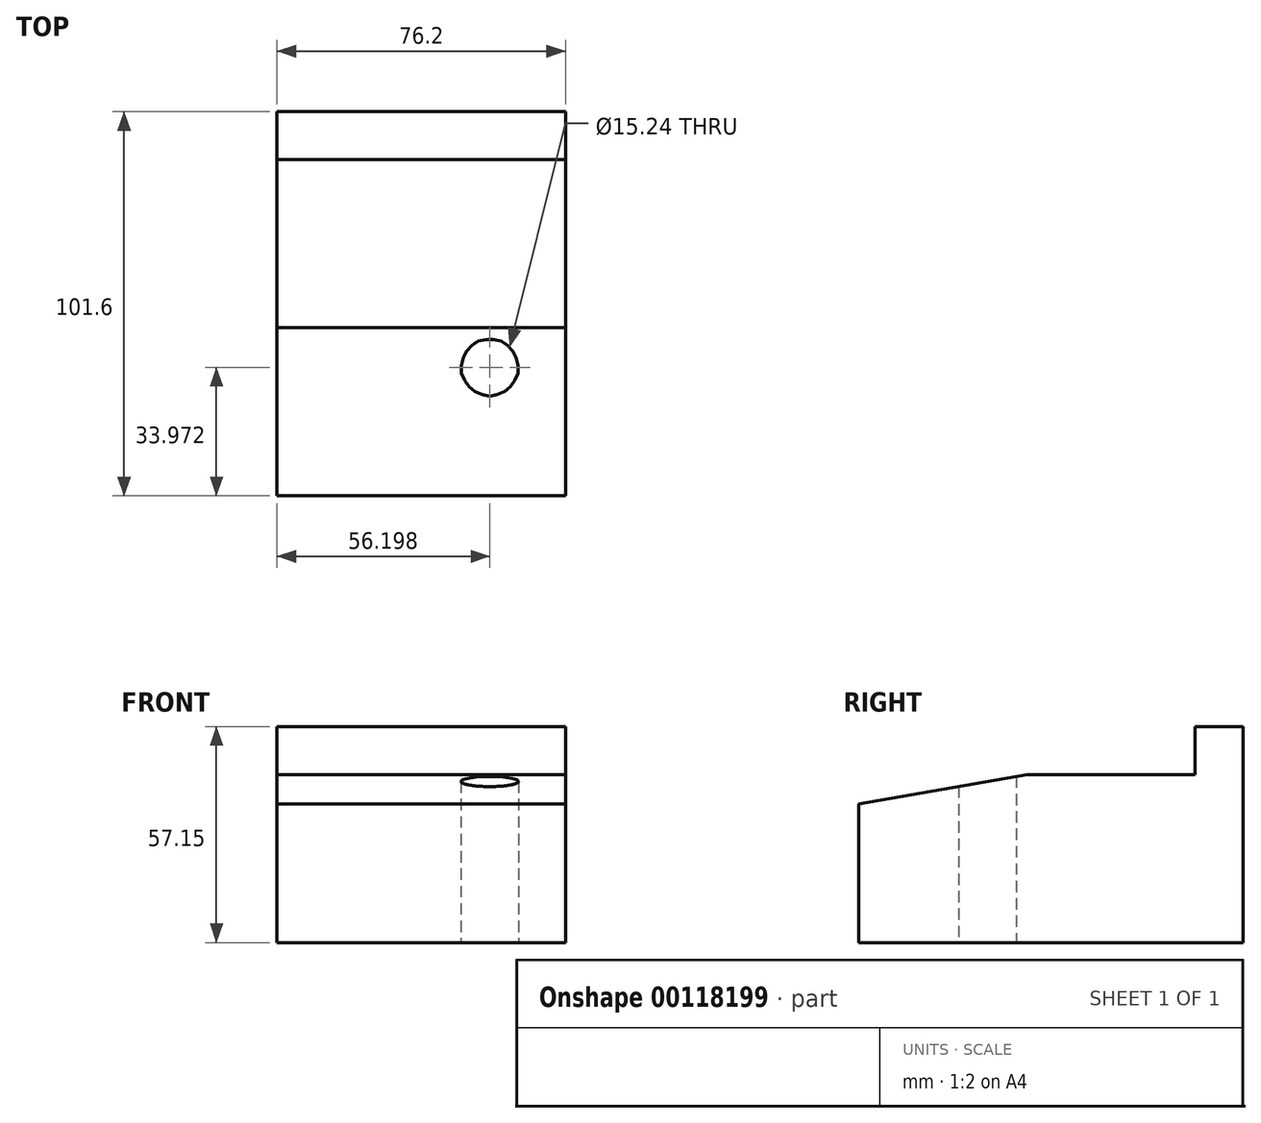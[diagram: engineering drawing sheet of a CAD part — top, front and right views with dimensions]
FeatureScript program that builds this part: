
annotation { "Feature Type Name" : "Feature", "Feature Type Description" : "" }
export const myFeature = defineFeature(function(context is Context, id is Id, definition is map)
    precondition{}
    {
        {
            var Q0;
            Q0=qCreatedBy(makeId("Right.planeOp"),FACE);
            var sketch = newSketch(context, id + "F0", { "sketchPlane" : qUnion([Q0])});
            skLineSegment(sketch, "E0.bottom", {"start": v(0, 0) * mm, "end": v(-101.6, 0) * mm});
            skLineSegment(sketch, "E0.top", {"start": v(0, 57.15) * mm, "end": v(-12.7, 57.15) * mm});
            skLineSegment(sketch, "E0.left", {"start": v(0, 0) * mm, "end": v(0, 57.15) * mm});
            skLineSegment(sketch, "E0.right", {"start": v(-101.6, 0) * mm, "end": v(-101.6, 36.61) * mm});
            skLineSegment(sketch, "E1", {"start": v(-12.7, 57.15) * mm, "end": v(-12.7, 44.48) * mm});
            skLineSegment(sketch, "E2", {"start": v(-12.7, 44.45) * mm, "end": v(-57.15, 44.45) * mm});
            skLineSegment(sketch, "E3", {"start": v(-12.7, 44.48) * mm, "end": v(-12.7, 44.45) * mm});
            skLineSegment(sketch, "E4", {"start": v(-57.15, 44.45) * mm, "end": v(-101.6, 36.61) * mm});
            skSolve(sketch);
        }
        {
            var Q0;
            Q0=makeQuery(id+"F0.imprint","IMPRINT",FACE,{"disambiguationData":[TD([[makeQuery(id+"F0.imprint","IMPRINT",EDGE,{"derivedFrom":sQuery(id+"F0.wireOp",EDGE,"E0.bottom")}),-1.0]])]});
            extrude(context, id + "F1", {"entities" : qUnion([Q0]), "oppositeDirection" : true, "depth" : 76.2 * mm});
        }
        {
            var Q0;
            Q0=qCreatedBy(makeId("Top.planeOp"),FACE);
            var sketch = newSketch(context, id + "F2", { "sketchPlane" : qUnion([Q0])});
            skCircle(sketch, "E5", {"center": v(-20, -67.63) * mm, "radius": 7.62 * mm});
            skSolve(sketch);
        }
        {
            var Q0;
            Q0 = qSketchRegion(id + "F2", true);
            extrude(context, id + "F3", {"entities" : qUnion([Q0]), "operationType" : NewBodyOperationType.REMOVE, "depth" : 50.8 * mm});
        }
    });
